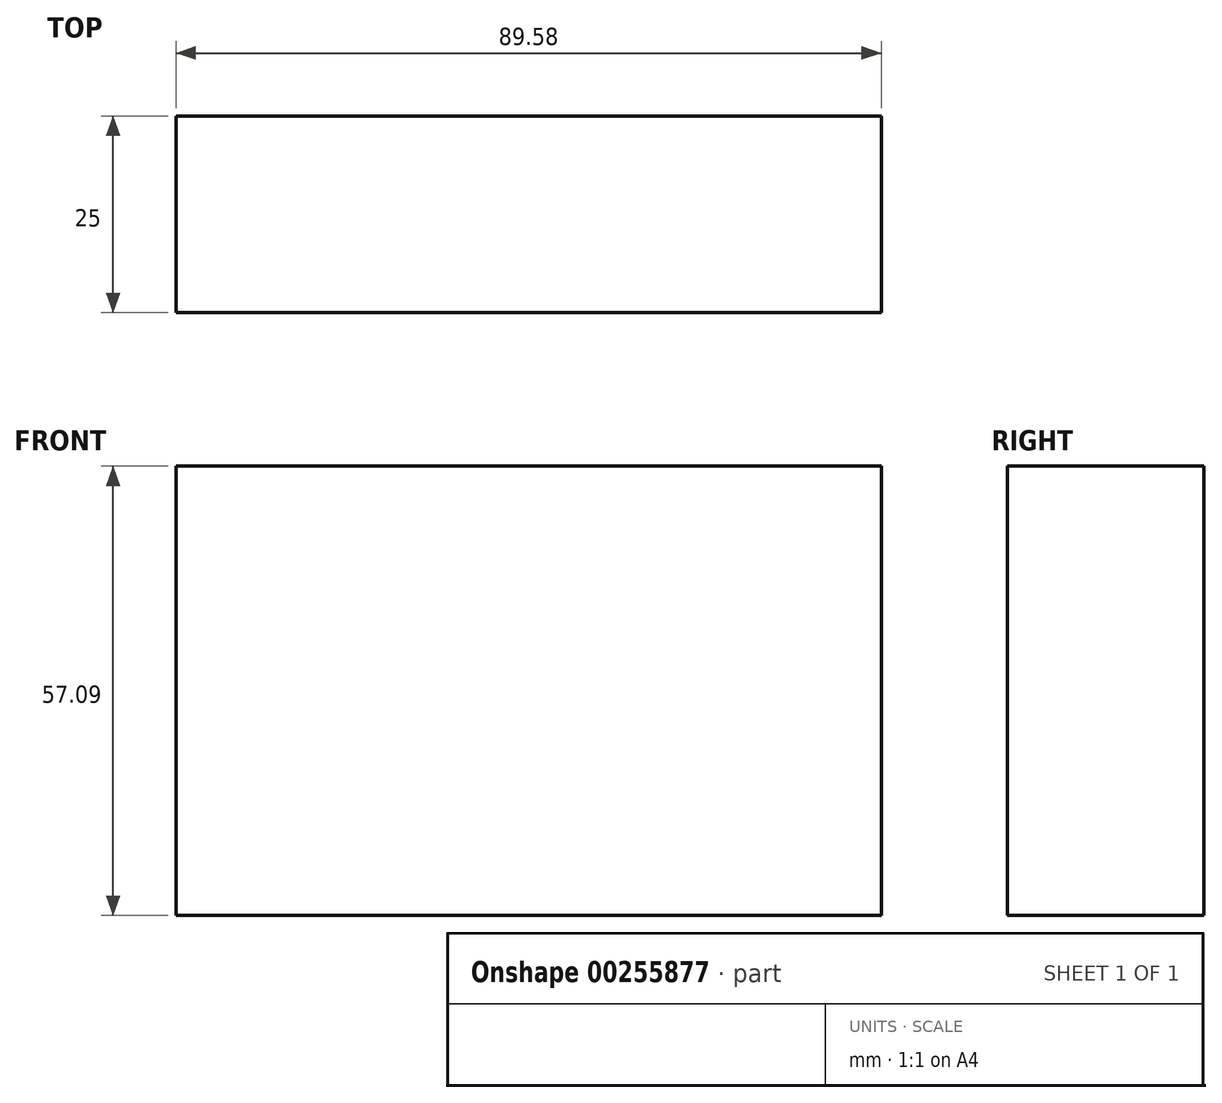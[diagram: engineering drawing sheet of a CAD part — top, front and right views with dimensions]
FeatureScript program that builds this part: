
annotation { "Feature Type Name" : "Feature", "Feature Type Description" : "" }
export const myFeature = defineFeature(function(context is Context, id is Id, definition is map)
    precondition{}
    {
        {
            var Q0;
            Q0=qCreatedBy(makeId("Front.planeOp"),FACE);
            var sketch = newSketch(context, id + "F0", { "sketchPlane" : qUnion([Q0])});
            skLineSegment(sketch, "E0.bottom", {"start": v(-97.7, 0) * mm, "end": v(-8.11, 0) * mm});
            skLineSegment(sketch, "E0.top", {"start": v(-97.7, 57.09) * mm, "end": v(-8.11, 57.09) * mm});
            skLineSegment(sketch, "E0.left", {"start": v(-97.7, 0) * mm, "end": v(-97.7, 57.09) * mm});
            skLineSegment(sketch, "E0.right", {"start": v(-8.11, 0) * mm, "end": v(-8.11, 57.09) * mm});
            skPoint(sketch, "E0.middle", {"position": v(-52.9, 28.54) * mm});
            skSolve(sketch);
        }
        {
            var Q0;
            Q0 = qSketchRegion(id + "F0", true);
            extrude(context, id + "F1", {"entities" : qUnion([Q0]), "depth" : 25 * mm});
        }
    });
